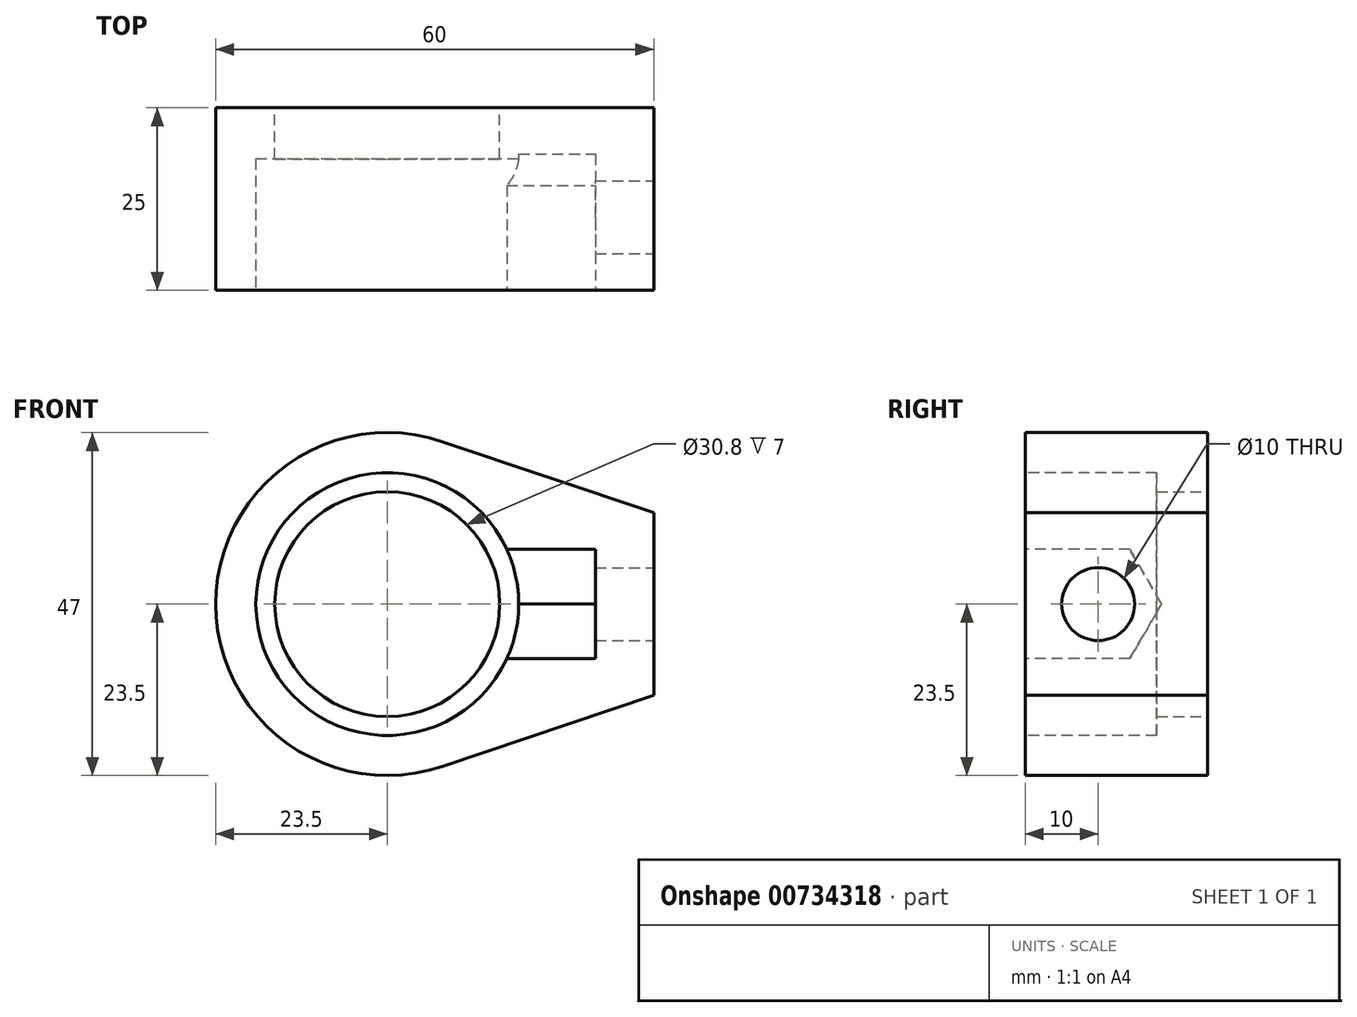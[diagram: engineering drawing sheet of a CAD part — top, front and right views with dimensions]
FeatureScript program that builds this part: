
annotation { "Feature Type Name" : "Feature", "Feature Type Description" : "" }
export const myFeature = defineFeature(function(context is Context, id is Id, definition is map)
    precondition{}
    {
        {
            var Q0;
            Q0=qCreatedBy(makeId("Front.planeOp"),FACE);
            var sketch = newSketch(context, id + "F0", { "sketchPlane" : qUnion([Q0])});
            skLineSegment(sketch, "E0", {"start": v(60, 47) * mm, "end": v(0, 47) * mm, "construction": true});
            skLineSegment(sketch, "E1", {"start": v(0, 47) * mm, "end": v(0, 0) * mm, "construction": true});
            skLineSegment(sketch, "E2", {"start": v(60, 23.5) * mm, "end": v(60, 36) * mm});
            skLineSegment(sketch, "E3", {"start": v(60, 23.5) * mm, "end": v(60, 11) * mm});
            skArc(sketch, "E4", {"start": v(31, 45.77) * mm, "mid": v(0, 23.5) * mm, "end": v(31, 1.23) * mm});
            skLineSegment(sketch, "E5", {"start": v(60, 36) * mm, "end": v(31, 45.77) * mm});
            skLineSegment(sketch, "E6", {"start": v(60, 11) * mm, "end": v(31, 1.23) * mm});
            skSolve(sketch);
        }
        {
            var Q0;
            Q0 = qSketchRegion(id + "F0", true);
            extrude(context, id + "F1", {"entities" : qUnion([Q0]), "depth" : 25 * mm, "offsetDistance" : 25 * mm});
        }
        {
            var Q0;
            Q0=makeQuery(id+"F1.opExtrude","CAP_FACE",FACE,{"disambiguationData":[OSD([sQuery(id+"F0.wireOp",EDGE,"E2"),sQuery(id+"F0.wireOp",EDGE,"E3"),sQuery(id+"F0.wireOp",EDGE,"E4"),sQuery(id+"F0.wireOp",EDGE,"E5"),sQuery(id+"F0.wireOp",EDGE,"E6")])],"isStart":false});
            var sketch = newSketch(context, id + "F2", { "sketchPlane" : qUnion([Q0])});
            skLineSegment(sketch, "E7", {"start": v(60, 23.5) * mm, "end": v(0, 23.5) * mm, "construction": true});
            skLineSegment(sketch, "E8", {"start": v(23.5, 23.5) * mm, "end": v(23.5, 0) * mm, "construction": true});
            skCircle(sketch, "E9", {"center": v(23.5, 23.5) * mm, "radius": 18 * mm});
            skSolve(sketch);
        }
        {
            var Q0;
            Q0=makeQuery(id+"F2.imprint","IMPRINT",FACE,{"disambiguationData":[TD([[makeQuery(id+"F2.imprint","IMPRINT",EDGE,{"derivedFrom":sQuery(id+"F2.wireOp",EDGE,"E9")}),1.0]])]});
            extrude(context, id + "F3", {"entities" : qUnion([Q0]), "operationType" : NewBodyOperationType.REMOVE, "oppositeDirection" : true, "depth" : 18 * mm, "offsetDistance" : 25 * mm});
        }
        {
            var Q0;
            Q0=makeQuery(id+"F1.opExtrude","CAP_FACE",FACE,{"disambiguationData":[OSD([sQuery(id+"F0.wireOp",EDGE,"E2"),sQuery(id+"F0.wireOp",EDGE,"E3"),sQuery(id+"F0.wireOp",EDGE,"E4"),sQuery(id+"F0.wireOp",EDGE,"E5"),sQuery(id+"F0.wireOp",EDGE,"E6")])],"isStart":true});
            var sketch = newSketch(context, id + "F4", { "sketchPlane" : qUnion([Q0])});
            skLineSegment(sketch, "E10", {"start": v(-23.5, 23.5) * mm, "end": v(-23.5, 0) * mm, "construction": true});
            skCircle(sketch, "E11", {"center": v(-23.5, 23.5) * mm, "radius": 15.4 * mm});
            skSolve(sketch);
        }
        {
            var Q0;
            Q0=makeQuery(id+"F4.imprint","IMPRINT",FACE,{"disambiguationData":[TD([[makeQuery(id+"F4.imprint","IMPRINT",EDGE,{"derivedFrom":sQuery(id+"F4.wireOp",EDGE,"E11")}),1.0]])]});
            var Q1;
            Q1=sQuery(id+"F4.wireOp",EDGE,"E10");
            var Q2;
            Q2=sQuery(id+"F4.wireOp",EDGE,"E11");
            extrude(context, id + "F5", {"entities" : qUnion([Q0]), "operationType" : NewBodyOperationType.REMOVE, "surfaceEntities" : qUnion([Q1, Q2]), "oppositeDirection" : true, "depth" : 7 * mm, "offsetDistance" : 25 * mm});
        }
        {
            var Q0;
            Q0=makeQuery(id+"F1.opExtrude","SWEPT_FACE",FACE,{"disambiguationData":[OSD([sQuery(id+"F0.wireOp",EDGE,"E2"),sQuery(id+"F0.wireOp",EDGE,"E3")])]});
            var sketch = newSketch(context, id + "F6", { "sketchPlane" : qUnion([Q0])});
            skCircle(sketch, "E12", {"center": v(-15, 23.5) * mm, "radius": 5 * mm});
            skLineSegment(sketch, "E13", {"start": v(-25, 23.5) * mm, "end": v(-20, 23.5) * mm, "construction": true});
            skSolve(sketch);
        }
        {
            var Q0;
            Q0=makeQuery(id+"F6.imprint","IMPRINT",FACE,{"disambiguationData":[TD([[makeQuery(id+"F6.imprint","IMPRINT",EDGE,{"derivedFrom":sQuery(id+"F6.wireOp",EDGE,"E12")}),1.0]])]});
            extrude(context, id + "F7", {"entities" : qUnion([Q0]), "operationType" : NewBodyOperationType.REMOVE, "oppositeDirection" : true, "depth" : 25 * mm, "offsetDistance" : 25 * mm});
        }
        {
            var Q0;
            Q0=makeQuery(id+"F1.opExtrude","CAP_FACE",FACE,{"disambiguationData":[OSD([sQuery(id+"F0.wireOp",EDGE,"E2"),sQuery(id+"F0.wireOp",EDGE,"E3"),sQuery(id+"F0.wireOp",EDGE,"E4"),sQuery(id+"F0.wireOp",EDGE,"E5"),sQuery(id+"F0.wireOp",EDGE,"E6")])],"isStart":false});
            var sketch = newSketch(context, id + "F8", { "sketchPlane" : qUnion([Q0])});
            skLineSegment(sketch, "E14", {"start": v(60, 23.5) * mm, "end": v(52, 23.5) * mm});
            skLineSegment(sketch, "E15", {"start": v(52, 23.5) * mm, "end": v(52, 16) * mm});
            skLineSegment(sketch, "E16", {"start": v(52, 23.5) * mm, "end": v(52, 31) * mm});
            skLineSegment(sketch, "E17", {"start": v(52, 16) * mm, "end": v(39.86, 16) * mm});
            skLineSegment(sketch, "E18", {"start": v(52, 31) * mm, "end": v(39.86, 31) * mm});
            skSolve(sketch);
        }
        {
            var Q0;
            Q0=makeQuery(id+"F8.imprint","IMPRINT",FACE,{"disambiguationData":[TD([[makeQuery(id+"F8.imprint","IMPRINT",EDGE,{"derivedFrom":sQuery(id+"F8.wireOp",EDGE,"E15")}),-1.0]])]});
            extrude(context, id + "F9", {"entities" : qUnion([Q0]), "operationType" : NewBodyOperationType.REMOVE, "oppositeDirection" : true, "depth" : 22 * mm, "offsetDistance" : 25 * mm});
        }
        {
            var Q0;
            Q0=makeQuery(id+"F9.boolean.opBoolean","COPY",FACE,{"derivedFrom":makeQuery(id+"F9.opExtrude","SWEPT_FACE",FACE,{"disambiguationData":[OSD([sQuery(id+"F8.wireOp",EDGE,"E15"),sQuery(id+"F8.wireOp",EDGE,"E16")])]})});
            var sketch = newSketch(context, id + "F10", { "sketchPlane" : qUnion([Q0])});
            skLineSegment(sketch, "E19", {"start": v(25, 23.5) * mm, "end": v(3, 23.5) * mm, "construction": true});
            skLineSegment(sketch, "E20", {"start": v(15, 23.5) * mm, "end": v(15, 16) * mm, "construction": true});
            skCircle(sketch, "E21.cCircle", {"center": v(15, 23.5) * mm, "radius": 7.5 * mm, "construction": true});
            skLineSegment(sketch, "E21.0", {"start": v(19.33, 16) * mm, "end": v(10.67, 16) * mm});
            skLineSegment(sketch, "E21.1", {"start": v(10.67, 16) * mm, "end": v(6.34, 23.5) * mm});
            skLineSegment(sketch, "E21.2", {"start": v(6.34, 23.5) * mm, "end": v(10.67, 31) * mm});
            skLineSegment(sketch, "E21.3", {"start": v(10.67, 31) * mm, "end": v(19.33, 31) * mm});
            skLineSegment(sketch, "E21.4", {"start": v(19.33, 31) * mm, "end": v(23.66, 23.5) * mm});
            skLineSegment(sketch, "E21.5", {"start": v(23.66, 23.5) * mm, "end": v(19.33, 16) * mm});
            skPoint(sketch, "E21.0.midPoint", {"position": v(15, 16) * mm});
            skSolve(sketch);
        }
        {
            var Q0;
            {var subQ4=sQuery(id+"F10.wireOp",EDGE,"E21.1");Q0=makeQuery(id+"F10.imprint","IMPRINT",FACE,{"disambiguationData":[TD([[makeQuery(id+"F10.imprint","IMPRINT",EDGE,{"derivedFrom":subQ4}),1.0]])]});}
            var Q1;
            Q1=makeQuery(id+"F9.boolean.opBoolean","COPY",FACE,{"derivedFrom":makeQuery(id+"F9.opExtrude","SWEPT_FACE",FACE,{"disambiguationData":[OSD([sQuery(id+"F2.wireOp",EDGE,"E9")])]})});
            extrude(context, id + "F11", {"entities" : qUnion([Q0]), "operationType" : NewBodyOperationType.ADD, "endBound" : BoundingType.UP_TO_SURFACE, "depth" : 25 * mm, "endBoundEntityFace" : qUnion([Q1]), "offsetDistance" : 25 * mm});
        }
    });
